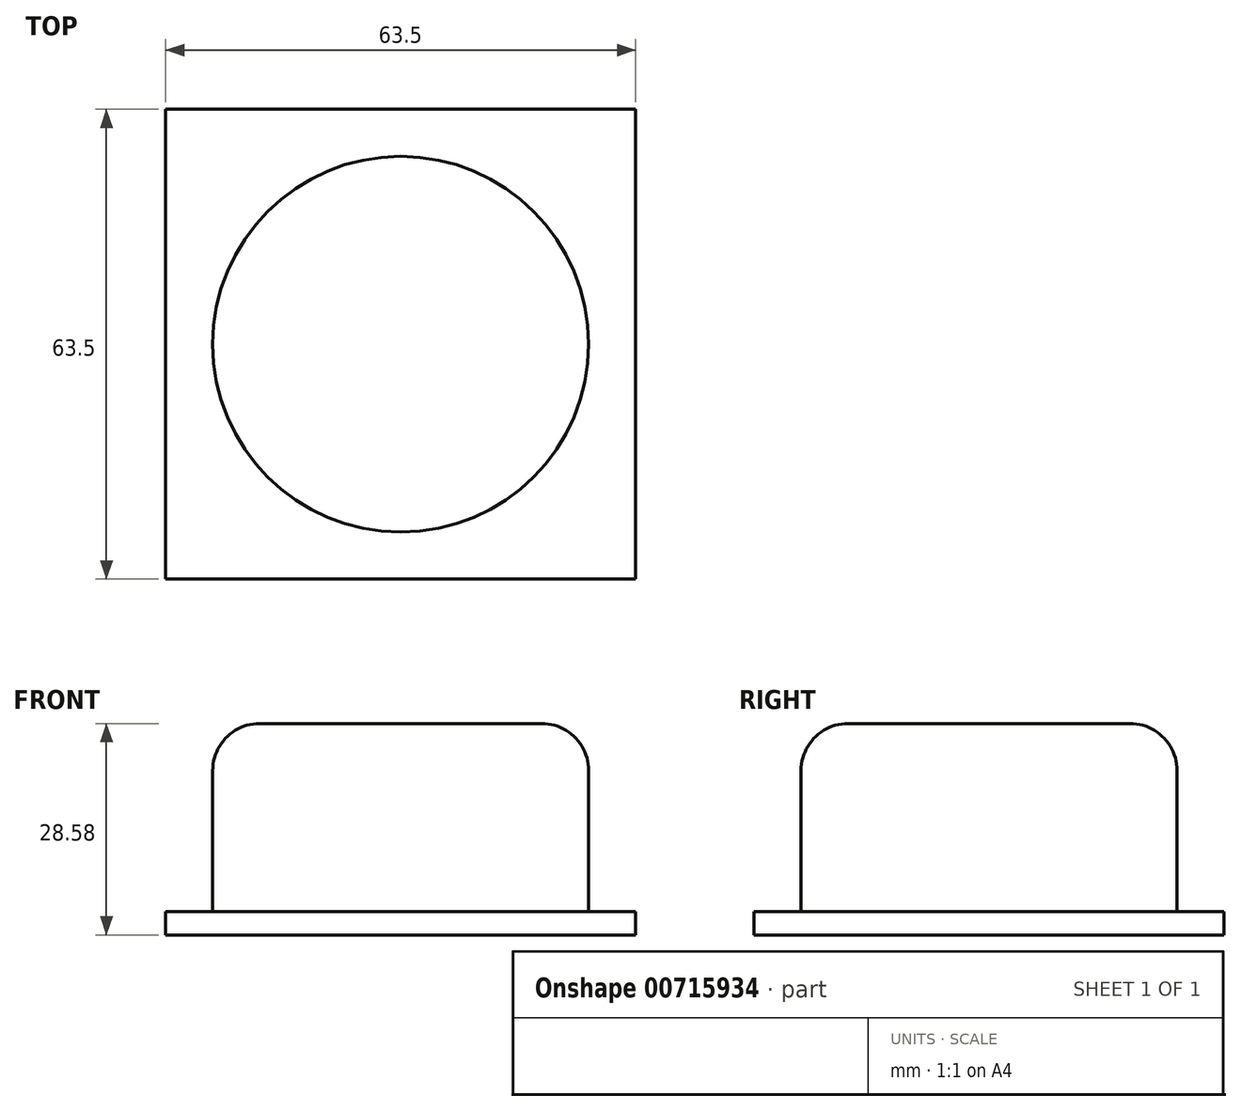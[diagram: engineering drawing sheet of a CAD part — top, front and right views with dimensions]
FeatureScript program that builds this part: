
annotation { "Feature Type Name" : "Feature", "Feature Type Description" : "" }
export const myFeature = defineFeature(function(context is Context, id is Id, definition is map)
    precondition{}
    {
        {
            var Q0;
            Q0=qCreatedBy(makeId("Top.planeOp"),FACE);
            var sketch = newSketch(context, id + "F0", { "sketchPlane" : qUnion([Q0])});
            skLineSegment(sketch, "E0.bottom", {"start": v(-31.75, 31.75) * mm, "end": v(31.75, 31.75) * mm});
            skLineSegment(sketch, "E0.top", {"start": v(-31.75, -31.75) * mm, "end": v(31.75, -31.75) * mm});
            skLineSegment(sketch, "E0.left", {"start": v(-31.75, 31.75) * mm, "end": v(-31.75, -31.75) * mm});
            skLineSegment(sketch, "E0.right", {"start": v(31.75, 31.75) * mm, "end": v(31.75, -31.75) * mm});
            skPoint(sketch, "E0.middle", {"position": v(0, 0) * mm});
            skSolve(sketch);
        }
        {
            var Q0;
            Q0=makeQuery(id+"F0.imprint","IMPRINT",FACE,{"disambiguationData":[TD([[makeQuery(id+"F0.imprint","IMPRINT",EDGE,{"derivedFrom":sQuery(id+"F0.wireOp",EDGE,"E0.bottom")}),-1.0]])]});
            extrude(context, id + "F1", {"entities" : qUnion([Q0]), "depth" : 3.17 * mm, "offsetDistance" : 25.4 * mm});
        }
        {
            var Q0;
            Q0=makeQuery(id+"F1.opExtrude","CAP_FACE",FACE,{"disambiguationData":[OSD([sQuery(id+"F0.wireOp",EDGE,"E0.bottom"),sQuery(id+"F0.wireOp",EDGE,"E0.top"),sQuery(id+"F0.wireOp",EDGE,"E0.left"),sQuery(id+"F0.wireOp",EDGE,"E0.right")])],"isStart":false});
            var sketch = newSketch(context, id + "F2", { "sketchPlane" : qUnion([Q0])});
            skCircle(sketch, "E1", {"center": v(0, 0) * mm, "radius": 25.4 * mm});
            skSolve(sketch);
        }
        {
            var Q0;
            Q0 = qSketchRegion(id + "F2", true);
            extrude(context, id + "F3", {"entities" : qUnion([Q0]), "operationType" : NewBodyOperationType.ADD, "depth" : 25.4 * mm, "offsetDistance" : 25.4 * mm});
        }
        {
            var Q0;
            Q0=makeQuery(id+"F3.opExtrude","CAP_FACE",FACE,{"disambiguationData":[OSD([sQuery(id+"F2.wireOp",EDGE,"E1")])],"isStart":false});
            fillet(context, id + "F4", {"entities" : qUnion([Q0]), "radius" : 6.35 * mm, "tangentPropagation" : true, "allowEdgeOverflow" : false});
        }
    });
